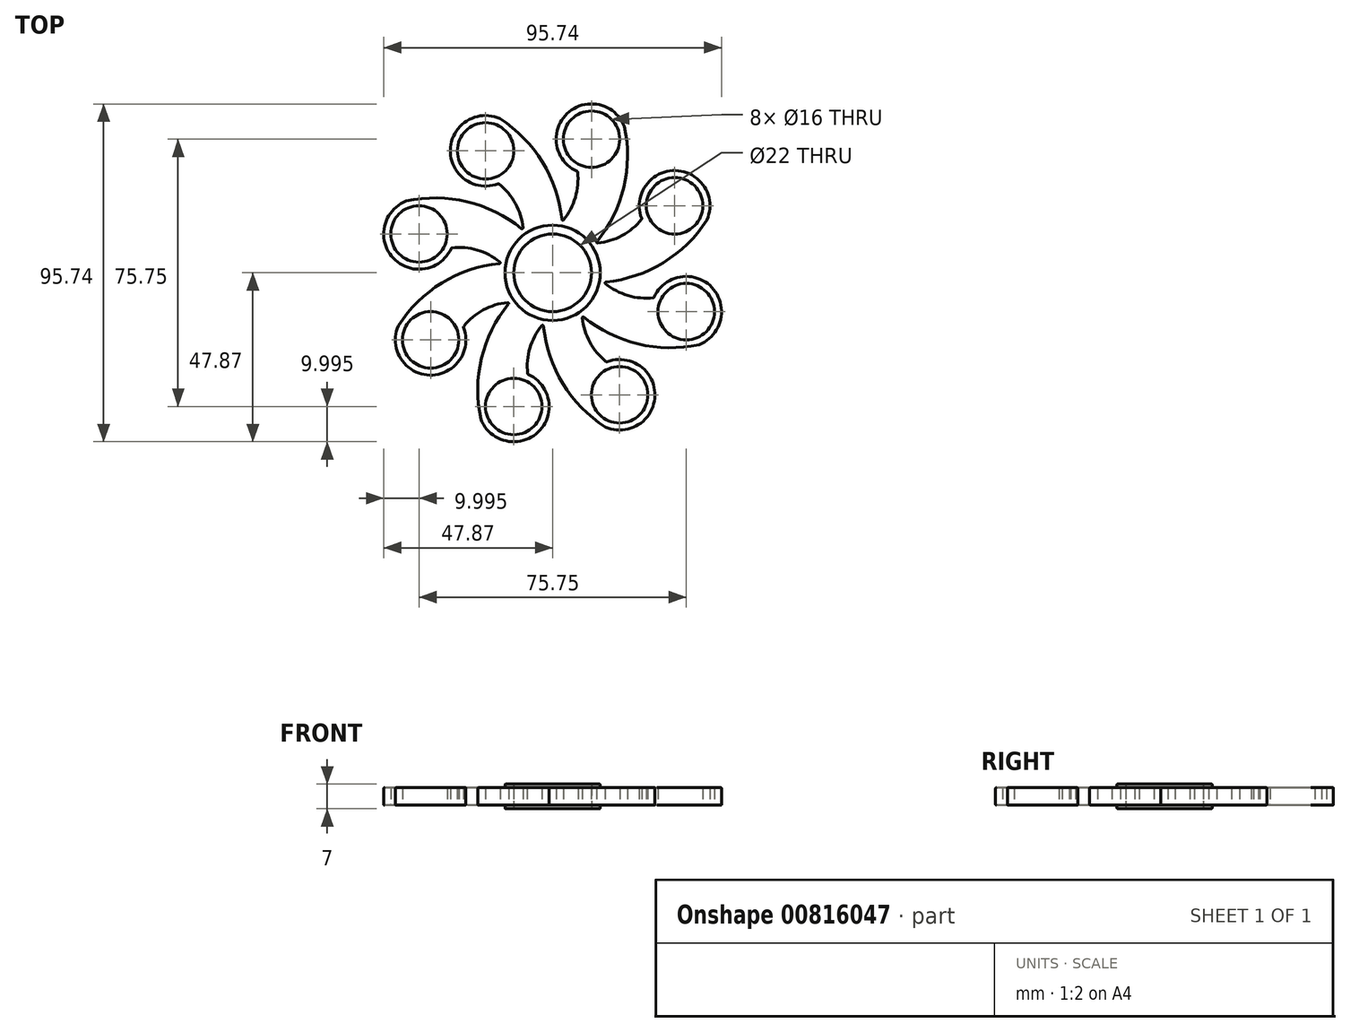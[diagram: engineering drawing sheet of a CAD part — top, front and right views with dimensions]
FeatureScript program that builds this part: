
annotation { "Feature Type Name" : "Feature", "Feature Type Description" : "" }
export const myFeature = defineFeature(function(context is Context, id is Id, definition is map)
    precondition{}
    {
        {
            var Q0;
            Q0=qCreatedBy(makeId("Top.planeOp"),FACE);
            var sketch = newSketch(context, id + "F0", { "sketchPlane" : qUnion([Q0])});
            skArc(sketch, "E0", {"start": v(-1.64, 10.88) * mm, "mid": v(-7.34, 8.2) * mm, "end": v(-10.63, 2.82) * mm});
            skCircle(sketch, "E1", {"center": v(0, 0) * mm, "radius": 11 * mm});
            skCircle(sketch, "E2", {"center": v(11.02, 37.87) * mm, "radius": 8 * mm});
            skPoint(sketch, "E3.start.orphan", {"position": v(0, 46.5) * mm});
            skArc(sketch, "E4", {"start": v(20.34, 41.5) * mm, "mid": v(4.08, 45.07) * mm, "end": v(7.06, 28.7) * mm});
            skArc(sketch, "E5", {"start": v(12.14, 8.36) * mm, "mid": v(20.1, 23.97) * mm, "end": v(20.34, 41.5) * mm});
            skArc(sketch, "E6", {"start": v(2.68, 14.5) * mm, "mid": v(6.38, 21.13) * mm, "end": v(7.06, 28.7) * mm});
            skArc(sketch, "E7.1.0", {"start": v(-14.96, 43.72) * mm, "mid": v(-29, 34.75) * mm, "end": v(-15.3, 25.28) * mm});
            skArc(sketch, "E7.1.1", {"start": v(2.68, 14.5) * mm, "mid": v(-2.74, 31.16) * mm, "end": v(-14.96, 43.72) * mm});
            skArc(sketch, "E7.1.2", {"start": v(-8.36, 12.14) * mm, "mid": v(-10.43, 19.45) * mm, "end": v(-15.3, 25.28) * mm});
            skCircle(sketch, "E7.1.3", {"center": v(-19, 34.57) * mm, "radius": 8 * mm});
            skArc(sketch, "E7.2.0", {"start": v(-41.5, 20.34) * mm, "mid": v(-45.07, 4.08) * mm, "end": v(-28.7, 7.06) * mm});
            skArc(sketch, "E7.2.1", {"start": v(-8.36, 12.14) * mm, "mid": v(-23.97, 20.1) * mm, "end": v(-41.5, 20.34) * mm});
            skArc(sketch, "E7.2.2", {"start": v(-14.5, 2.68) * mm, "mid": v(-21.13, 6.38) * mm, "end": v(-28.7, 7.06) * mm});
            skCircle(sketch, "E7.2.3", {"center": v(-37.87, 11.02) * mm, "radius": 8 * mm});
            skArc(sketch, "E7.3.0", {"start": v(-43.72, -14.96) * mm, "mid": v(-34.75, -29) * mm, "end": v(-25.28, -15.3) * mm});
            skArc(sketch, "E7.3.1", {"start": v(-14.5, 2.68) * mm, "mid": v(-31.16, -2.74) * mm, "end": v(-43.72, -14.96) * mm});
            skArc(sketch, "E7.3.2", {"start": v(-12.14, -8.36) * mm, "mid": v(-19.45, -10.43) * mm, "end": v(-25.28, -15.3) * mm});
            skCircle(sketch, "E7.3.3", {"center": v(-34.57, -19) * mm, "radius": 8 * mm});
            skArc(sketch, "E7.4.0", {"start": v(-20.34, -41.5) * mm, "mid": v(-4.08, -45.07) * mm, "end": v(-7.06, -28.7) * mm});
            skArc(sketch, "E7.4.1", {"start": v(-12.14, -8.36) * mm, "mid": v(-20.1, -23.97) * mm, "end": v(-20.34, -41.5) * mm});
            skArc(sketch, "E7.4.2", {"start": v(-2.68, -14.5) * mm, "mid": v(-6.38, -21.13) * mm, "end": v(-7.06, -28.7) * mm});
            skCircle(sketch, "E7.4.3", {"center": v(-11.02, -37.87) * mm, "radius": 8 * mm});
            skArc(sketch, "E7.5.0", {"start": v(14.96, -43.72) * mm, "mid": v(29, -34.75) * mm, "end": v(15.3, -25.28) * mm});
            skArc(sketch, "E7.5.1", {"start": v(-2.68, -14.5) * mm, "mid": v(2.74, -31.16) * mm, "end": v(14.96, -43.72) * mm});
            skArc(sketch, "E7.5.2", {"start": v(8.36, -12.14) * mm, "mid": v(10.43, -19.45) * mm, "end": v(15.3, -25.28) * mm});
            skCircle(sketch, "E7.5.3", {"center": v(19, -34.57) * mm, "radius": 8 * mm});
            skArc(sketch, "E7.6.0", {"start": v(41.5, -20.34) * mm, "mid": v(45.07, -4.08) * mm, "end": v(28.7, -7.06) * mm});
            skArc(sketch, "E7.6.1", {"start": v(8.36, -12.14) * mm, "mid": v(23.97, -20.1) * mm, "end": v(41.5, -20.34) * mm});
            skArc(sketch, "E7.6.2", {"start": v(14.5, -2.68) * mm, "mid": v(21.13, -6.38) * mm, "end": v(28.7, -7.06) * mm});
            skCircle(sketch, "E7.6.3", {"center": v(37.87, -11.02) * mm, "radius": 8 * mm});
            skArc(sketch, "E7.7.0", {"start": v(43.72, 14.96) * mm, "mid": v(34.75, 29) * mm, "end": v(25.28, 15.3) * mm});
            skArc(sketch, "E7.7.1", {"start": v(14.5, -2.68) * mm, "mid": v(31.16, 2.74) * mm, "end": v(43.72, 14.96) * mm});
            skArc(sketch, "E7.7.2", {"start": v(12.14, 8.36) * mm, "mid": v(19.45, 10.43) * mm, "end": v(25.28, 15.3) * mm});
            skCircle(sketch, "E7.7.3", {"center": v(34.57, 19) * mm, "radius": 8 * mm});
            skArc(sketch, "E8.trimOffspring", {"start": v(-8.85, 6.53) * mm, "mid": v(-9.92, 4.76) * mm, "end": v(-10.63, 2.82) * mm});
            skArc(sketch, "E9.trimOffspring", {"start": v(-10.88, -1.64) * mm, "mid": v(10.98, -0.6) * mm, "end": v(-10.63, 2.82) * mm});
            skArc(sketch, "E10.trimOffspring", {"start": v(-6.53, -8.85) * mm, "mid": v(8.2, 7.34) * mm, "end": v(-9.51, -5.53) * mm});
            skArc(sketch, "E11.trimOffspring", {"start": v(1.64, -10.88) * mm, "mid": v(0.6, 10.98) * mm, "end": v(-2.82, -10.63) * mm});
            skArc(sketch, "E12.trimOffspring", {"start": v(8.85, -6.53) * mm, "mid": v(4.76, 9.92) * mm, "end": v(-10.63, 2.82) * mm});
            skArc(sketch, "E13.trimOffspring", {"start": v(10.88, 1.64) * mm, "mid": v(0.6, 10.98) * mm, "end": v(-10.63, 2.82) * mm});
            skArc(sketch, "E14.trimOffspring", {"start": v(2.82, 10.63) * mm, "mid": v(-1.47, 10.9) * mm, "end": v(-5.53, 9.51) * mm});
            skArc(sketch, "E15.trimOffspring", {"start": v(-10.88, -1.64) * mm, "mid": v(-4.76, -9.92) * mm, "end": v(5.53, -9.51) * mm});
            skArc(sketch, "E16.trimOffspring", {"start": v(-10.88, -1.64) * mm, "mid": v(-0.6, -10.98) * mm, "end": v(10.63, -2.82) * mm});
            skSolve(sketch);
        }
        {
            var Q0;
            Q0 = qSketchRegion(id + "F0", true);
            extrude(context, id + "F1", {"entities" : qUnion([Q0]), "depth" : 5 * mm, "offsetDistance" : 25 * mm});
        }
        {
            var Q0;
            Q0=makeQuery(id+"F1.opExtrude","CAP_FACE",FACE,{"disambiguationData":[OSD([sQuery(id+"F0.wireOp",EDGE,"E1"),sQuery(id+"F0.wireOp",EDGE,"E2"),sQuery(id+"F0.wireOp",EDGE,"E4"),sQuery(id+"F0.wireOp",EDGE,"E5"),sQuery(id+"F0.wireOp",EDGE,"E6"),sQuery(id+"F0.wireOp",EDGE,"E7.1.0"),sQuery(id+"F0.wireOp",EDGE,"E7.1.1"),sQuery(id+"F0.wireOp",EDGE,"E7.1.2"),sQuery(id+"F0.wireOp",EDGE,"E7.1.3"),sQuery(id+"F0.wireOp",EDGE,"E7.2.0"),sQuery(id+"F0.wireOp",EDGE,"E7.2.1"),sQuery(id+"F0.wireOp",EDGE,"E7.2.2"),sQuery(id+"F0.wireOp",EDGE,"E7.2.3"),sQuery(id+"F0.wireOp",EDGE,"E7.3.0"),sQuery(id+"F0.wireOp",EDGE,"E7.3.1"),sQuery(id+"F0.wireOp",EDGE,"E7.3.2"),sQuery(id+"F0.wireOp",EDGE,"E7.3.3"),sQuery(id+"F0.wireOp",EDGE,"E7.4.0"),sQuery(id+"F0.wireOp",EDGE,"E7.4.1"),sQuery(id+"F0.wireOp",EDGE,"E7.4.2"),sQuery(id+"F0.wireOp",EDGE,"E7.4.3"),sQuery(id+"F0.wireOp",EDGE,"E7.5.0"),sQuery(id+"F0.wireOp",EDGE,"E7.5.1"),sQuery(id+"F0.wireOp",EDGE,"E7.5.2"),sQuery(id+"F0.wireOp",EDGE,"E7.5.3"),sQuery(id+"F0.wireOp",EDGE,"E7.6.0"),sQuery(id+"F0.wireOp",EDGE,"E7.6.1"),sQuery(id+"F0.wireOp",EDGE,"E7.6.2"),sQuery(id+"F0.wireOp",EDGE,"E7.6.3"),sQuery(id+"F0.wireOp",EDGE,"E7.7.0"),sQuery(id+"F0.wireOp",EDGE,"E7.7.1"),sQuery(id+"F0.wireOp",EDGE,"E7.7.2"),sQuery(id+"F0.wireOp",EDGE,"E7.7.3")])],"isStart":false});
            var sketch = newSketch(context, id + "F2", { "sketchPlane" : qUnion([Q0])});
            skCircle(sketch, "E17", {"center": v(0, 0) * mm, "radius": 11 * mm});
            skCircle(sketch, "E18", {"center": v(0, 0) * mm, "radius": 13.5 * mm});
            skSolve(sketch);
        }
        {
            var Q0;
            Q0 = qSketchRegion(id + "F2", true);
            extrude(context, id + "F3", {"entities" : qUnion([Q0]), "operationType" : NewBodyOperationType.ADD, "depth" : 1 * mm, "offsetDistance" : 25 * mm});
        }
        {
            var Q0;
            Q0=makeQuery(id+"F1.opExtrude","CAP_FACE",FACE,{"disambiguationData":[OSD([sQuery(id+"F0.wireOp",EDGE,"E1"),sQuery(id+"F0.wireOp",EDGE,"E2"),sQuery(id+"F0.wireOp",EDGE,"E4"),sQuery(id+"F0.wireOp",EDGE,"E5"),sQuery(id+"F0.wireOp",EDGE,"E6"),sQuery(id+"F0.wireOp",EDGE,"E7.1.0"),sQuery(id+"F0.wireOp",EDGE,"E7.1.1"),sQuery(id+"F0.wireOp",EDGE,"E7.1.2"),sQuery(id+"F0.wireOp",EDGE,"E7.1.3"),sQuery(id+"F0.wireOp",EDGE,"E7.2.0"),sQuery(id+"F0.wireOp",EDGE,"E7.2.1"),sQuery(id+"F0.wireOp",EDGE,"E7.2.2"),sQuery(id+"F0.wireOp",EDGE,"E7.2.3"),sQuery(id+"F0.wireOp",EDGE,"E7.3.0"),sQuery(id+"F0.wireOp",EDGE,"E7.3.1"),sQuery(id+"F0.wireOp",EDGE,"E7.3.2"),sQuery(id+"F0.wireOp",EDGE,"E7.3.3"),sQuery(id+"F0.wireOp",EDGE,"E7.4.0"),sQuery(id+"F0.wireOp",EDGE,"E7.4.1"),sQuery(id+"F0.wireOp",EDGE,"E7.4.2"),sQuery(id+"F0.wireOp",EDGE,"E7.4.3"),sQuery(id+"F0.wireOp",EDGE,"E7.5.0"),sQuery(id+"F0.wireOp",EDGE,"E7.5.1"),sQuery(id+"F0.wireOp",EDGE,"E7.5.2"),sQuery(id+"F0.wireOp",EDGE,"E7.5.3"),sQuery(id+"F0.wireOp",EDGE,"E7.6.0"),sQuery(id+"F0.wireOp",EDGE,"E7.6.1"),sQuery(id+"F0.wireOp",EDGE,"E7.6.2"),sQuery(id+"F0.wireOp",EDGE,"E7.6.3"),sQuery(id+"F0.wireOp",EDGE,"E7.7.0"),sQuery(id+"F0.wireOp",EDGE,"E7.7.1"),sQuery(id+"F0.wireOp",EDGE,"E7.7.2"),sQuery(id+"F0.wireOp",EDGE,"E7.7.3")])],"isStart":true});
            var sketch = newSketch(context, id + "F4", { "sketchPlane" : qUnion([Q0])});
            skCircle(sketch, "E19", {"center": v(0, 0) * mm, "radius": 11 * mm});
            skCircle(sketch, "E20", {"center": v(0, 0) * mm, "radius": 13.5 * mm});
            skSolve(sketch);
        }
        {
            var Q0;
            Q0 = qSketchRegion(id + "F4", true);
            extrude(context, id + "F5", {"entities" : qUnion([Q0]), "operationType" : NewBodyOperationType.ADD, "depth" : 1 * mm, "offsetDistance" : 25 * mm});
        }
        {
            var Q0;
            Q0=makeQuery(id+"F1.opExtrude","SWEPT_FACE",FACE,{"disambiguationData":[OSD([sQuery(id+"F0.wireOp",EDGE,"E7.7.0")])]});
            var Q1;
            Q1=makeQuery(id+"F1.opExtrude","CAP_EDGE",EDGE,{"disambiguationData":[OSD([sQuery(id+"F0.wireOp",EDGE,"E7.3.3")])],"isStart":false});
            var Q2;
            Q2=makeQuery(id+"F1.opExtrude","CAP_EDGE",EDGE,{"disambiguationData":[OSD([sQuery(id+"F0.wireOp",EDGE,"E7.6.0")])],"isStart":false});
            var Q3;
            Q3=makeQuery(id+"F1.opExtrude","CAP_EDGE",EDGE,{"disambiguationData":[OSD([sQuery(id+"F0.wireOp",EDGE,"E7.3.0")])],"isStart":false});
            var Q4;
            Q4=makeQuery(id+"F1.opExtrude","CAP_EDGE",EDGE,{"disambiguationData":[OSD([sQuery(id+"F0.wireOp",EDGE,"E7.4.2")])],"isStart":false});
            var Q5;
            Q5=makeQuery(id+"F1.opExtrude","CAP_EDGE",EDGE,{"disambiguationData":[OSD([sQuery(id+"F0.wireOp",EDGE,"E7.3.2")])],"isStart":false});
            var Q6;
            Q6=makeQuery(id+"F1.opExtrude","CAP_EDGE",EDGE,{"disambiguationData":[OSD([sQuery(id+"F0.wireOp",EDGE,"E7.1.0")])],"isStart":false});
            var Q7;
            Q7=makeQuery(id+"F1.opExtrude","CAP_EDGE",EDGE,{"disambiguationData":[OSD([sQuery(id+"F0.wireOp",EDGE,"E7.3.1")])],"isStart":false});
            var Q8;
            Q8=makeQuery(id+"F1.opExtrude","SWEPT_FACE",FACE,{"disambiguationData":[OSD([sQuery(id+"F0.wireOp",EDGE,"E7.3.0")])]});
            var Q9;
            Q9=makeQuery(id+"F1.opExtrude","CAP_EDGE",EDGE,{"disambiguationData":[OSD([sQuery(id+"F0.wireOp",EDGE,"E7.5.2")])],"isStart":false});
            var Q10;
            Q10=makeQuery(id+"F1.opExtrude","SWEPT_FACE",FACE,{"disambiguationData":[OSD([sQuery(id+"F0.wireOp",EDGE,"E5")])]});
            var Q11;
            Q11=makeQuery(id+"F1.opExtrude","SWEPT_FACE",FACE,{"disambiguationData":[OSD([sQuery(id+"F0.wireOp",EDGE,"E7.4.3")])]});
            var Q12;
            Q12=makeQuery(id+"F3.opExtrude","CAP_EDGE",EDGE,{"disambiguationData":[OSD([sQuery(id+"F2.wireOp",EDGE,"E18")])],"isStart":false});
            var Q13;
            Q13=makeQuery(id+"F1.opExtrude","SWEPT_FACE",FACE,{"disambiguationData":[OSD([sQuery(id+"F0.wireOp",EDGE,"E7.6.1")])]});
            var Q14;
            Q14=makeQuery(id+"F1.opExtrude","SWEPT_FACE",FACE,{"disambiguationData":[OSD([sQuery(id+"F0.wireOp",EDGE,"E7.5.0")])]});
            var Q15;
            Q15=makeQuery(id+"F3.opExtrude","SWEPT_FACE",FACE,{"disambiguationData":[OSD([sQuery(id+"F2.wireOp",EDGE,"E18")])]});
            var Q16;
            Q16=makeQuery(id+"F1.opExtrude","SWEPT_FACE",FACE,{"disambiguationData":[OSD([sQuery(id+"F0.wireOp",EDGE,"E7.3.3")])]});
            var Q17;
            Q17=makeQuery(id+"F1.opExtrude","SWEPT_FACE",FACE,{"disambiguationData":[OSD([sQuery(id+"F0.wireOp",EDGE,"E7.7.1")])]});
            var Q18;
            Q18=makeQuery(id+"F1.opExtrude","CAP_FACE",FACE,{"disambiguationData":[OSD([sQuery(id+"F0.wireOp",EDGE,"E1"),sQuery(id+"F0.wireOp",EDGE,"E2"),sQuery(id+"F0.wireOp",EDGE,"E4"),sQuery(id+"F0.wireOp",EDGE,"E5"),sQuery(id+"F0.wireOp",EDGE,"E6"),sQuery(id+"F0.wireOp",EDGE,"E7.1.0"),sQuery(id+"F0.wireOp",EDGE,"E7.1.1"),sQuery(id+"F0.wireOp",EDGE,"E7.1.2"),sQuery(id+"F0.wireOp",EDGE,"E7.1.3"),sQuery(id+"F0.wireOp",EDGE,"E7.2.0"),sQuery(id+"F0.wireOp",EDGE,"E7.2.1"),sQuery(id+"F0.wireOp",EDGE,"E7.2.2"),sQuery(id+"F0.wireOp",EDGE,"E7.2.3"),sQuery(id+"F0.wireOp",EDGE,"E7.3.0"),sQuery(id+"F0.wireOp",EDGE,"E7.3.1"),sQuery(id+"F0.wireOp",EDGE,"E7.3.2"),sQuery(id+"F0.wireOp",EDGE,"E7.3.3"),sQuery(id+"F0.wireOp",EDGE,"E7.4.0"),sQuery(id+"F0.wireOp",EDGE,"E7.4.1"),sQuery(id+"F0.wireOp",EDGE,"E7.4.2"),sQuery(id+"F0.wireOp",EDGE,"E7.4.3"),sQuery(id+"F0.wireOp",EDGE,"E7.5.0"),sQuery(id+"F0.wireOp",EDGE,"E7.5.1"),sQuery(id+"F0.wireOp",EDGE,"E7.5.2"),sQuery(id+"F0.wireOp",EDGE,"E7.5.3"),sQuery(id+"F0.wireOp",EDGE,"E7.6.0"),sQuery(id+"F0.wireOp",EDGE,"E7.6.1"),sQuery(id+"F0.wireOp",EDGE,"E7.6.2"),sQuery(id+"F0.wireOp",EDGE,"E7.6.3"),sQuery(id+"F0.wireOp",EDGE,"E7.7.0"),sQuery(id+"F0.wireOp",EDGE,"E7.7.1"),sQuery(id+"F0.wireOp",EDGE,"E7.7.2"),sQuery(id+"F0.wireOp",EDGE,"E7.7.3")])],"isStart":false});
            var Q19;
            Q19=makeQuery(id+"F1.opExtrude","SWEPT_FACE",FACE,{"disambiguationData":[OSD([sQuery(id+"F0.wireOp",EDGE,"E7.3.1")])]});
            var Q20;
            Q20=makeQuery(id+"F1.opExtrude","CAP_EDGE",EDGE,{"disambiguationData":[OSD([sQuery(id+"F0.wireOp",EDGE,"E7.7.2")])],"isStart":false});
            var Q21;
            Q21=makeQuery(id+"F1.opExtrude","CAP_EDGE",EDGE,{"disambiguationData":[OSD([sQuery(id+"F0.wireOp",EDGE,"E7.5.0")])],"isStart":false});
            var Q22;
            Q22=makeQuery(id+"F1.opExtrude","CAP_EDGE",EDGE,{"disambiguationData":[OSD([sQuery(id+"F0.wireOp",EDGE,"E7.1.1")])],"isStart":false});
            var Q23;
            Q23=makeQuery(id+"F1.opExtrude","CAP_EDGE",EDGE,{"disambiguationData":[OSD([sQuery(id+"F0.wireOp",EDGE,"E7.7.1")])],"isStart":false});
            var Q24;
            Q24=makeQuery(id+"F1.opExtrude","CAP_EDGE",EDGE,{"disambiguationData":[OSD([sQuery(id+"F0.wireOp",EDGE,"E7.6.1")])],"isStart":false});
            var Q25;
            Q25=makeQuery(id+"F1.opExtrude","CAP_EDGE",EDGE,{"disambiguationData":[OSD([sQuery(id+"F0.wireOp",EDGE,"E7.6.3")])],"isStart":false});
            var Q26;
            Q26=makeQuery(id+"F3.opExtrude","CAP_FACE",FACE,{"disambiguationData":[OSD([sQuery(id+"F2.wireOp",EDGE,"E17"),sQuery(id+"F2.wireOp",EDGE,"E18")])],"isStart":false});
            var Q27;
            Q27=makeQuery(id+"F1.opExtrude","SWEPT_FACE",FACE,{"disambiguationData":[OSD([sQuery(id+"F0.wireOp",EDGE,"E7.6.3")])]});
            var Q28;
            Q28=makeQuery(id+"F1.opExtrude","CAP_EDGE",EDGE,{"disambiguationData":[OSD([sQuery(id+"F0.wireOp",EDGE,"E7.4.1")])],"isStart":false});
            var Q29;
            Q29=makeQuery(id+"F1.opExtrude","SWEPT_FACE",FACE,{"disambiguationData":[OSD([sQuery(id+"F0.wireOp",EDGE,"E7.1.0")])]});
            var Q30;
            Q30=makeQuery(id+"F1.opExtrude","SWEPT_FACE",FACE,{"disambiguationData":[OSD([sQuery(id+"F0.wireOp",EDGE,"E7.6.0")])]});
            var Q31;
            Q31=makeQuery(id+"F1.opExtrude","SWEPT_FACE",FACE,{"disambiguationData":[OSD([sQuery(id+"F0.wireOp",EDGE,"E7.5.1")])]});
            var Q32;
            Q32=makeQuery(id+"F1.opExtrude","SWEPT_FACE",FACE,{"disambiguationData":[OSD([sQuery(id+"F0.wireOp",EDGE,"E7.4.0")])]});
            var Q33;
            Q33=makeQuery(id+"F1.opExtrude","SWEPT_FACE",FACE,{"disambiguationData":[OSD([sQuery(id+"F0.wireOp",EDGE,"E7.5.3")])]});
            var Q34;
            Q34=makeQuery(id+"F1.opExtrude","CAP_EDGE",EDGE,{"disambiguationData":[OSD([sQuery(id+"F0.wireOp",EDGE,"E7.2.1")])],"isStart":false});
            var Q35;
            Q35=makeQuery(id+"F1.opExtrude","SWEPT_FACE",FACE,{"disambiguationData":[OSD([sQuery(id+"F0.wireOp",EDGE,"E4")])]});
            var Q36;
            Q36=makeQuery(id+"F1.opExtrude","CAP_EDGE",EDGE,{"disambiguationData":[OSD([sQuery(id+"F0.wireOp",EDGE,"E4")])],"isStart":false});
            var Q37;
            Q37=makeQuery(id+"F1.opExtrude","SWEPT_FACE",FACE,{"disambiguationData":[OSD([sQuery(id+"F0.wireOp",EDGE,"E7.2.0")])]});
            var Q38;
            Q38=makeQuery(id+"F1.opExtrude","SWEPT_FACE",FACE,{"disambiguationData":[OSD([sQuery(id+"F0.wireOp",EDGE,"E7.2.3")])]});
            var Q39;
            Q39=makeQuery(id+"F1.opExtrude","SWEPT_FACE",FACE,{"disambiguationData":[OSD([sQuery(id+"F0.wireOp",EDGE,"E7.4.1")])]});
            var Q40;
            Q40=makeQuery(id+"F3.opExtrude","CAP_EDGE",EDGE,{"disambiguationData":[OSD([sQuery(id+"F2.wireOp",EDGE,"E17")])],"isStart":false});
            var Q41;
            Q41=makeQuery(id+"F1.opExtrude","CAP_EDGE",EDGE,{"disambiguationData":[OSD([sQuery(id+"F0.wireOp",EDGE,"E5")])],"isStart":false});
            var Q42;
            Q42=makeQuery(id+"F1.opExtrude","CAP_EDGE",EDGE,{"disambiguationData":[OSD([sQuery(id+"F0.wireOp",EDGE,"E7.6.2")])],"isStart":false});
            var Q43;
            Q43=makeQuery(id+"F1.opExtrude","CAP_EDGE",EDGE,{"disambiguationData":[OSD([sQuery(id+"F0.wireOp",EDGE,"E7.4.3")])],"isStart":false});
            var Q44;
            Q44=makeQuery(id+"F1.opExtrude","SWEPT_FACE",FACE,{"disambiguationData":[OSD([sQuery(id+"F0.wireOp",EDGE,"E7.1.1")])]});
            var Q45;
            Q45=makeQuery(id+"F1.opExtrude","CAP_EDGE",EDGE,{"disambiguationData":[OSD([sQuery(id+"F0.wireOp",EDGE,"E7.5.1")])],"isStart":false});
            var Q46;
            Q46=makeQuery(id+"F1.opExtrude","CAP_EDGE",EDGE,{"disambiguationData":[OSD([sQuery(id+"F0.wireOp",EDGE,"E6")])],"isStart":false});
            var Q47;
            Q47=makeQuery(id+"F1.opExtrude","SWEPT_FACE",FACE,{"disambiguationData":[OSD([sQuery(id+"F0.wireOp",EDGE,"E7.2.2")])]});
            var Q48;
            Q48=makeQuery(id+"F1.opExtrude","SWEPT_FACE",FACE,{"disambiguationData":[OSD([sQuery(id+"F0.wireOp",EDGE,"E6")])]});
            var Q49;
            Q49=makeQuery(id+"F1.opExtrude","CAP_EDGE",EDGE,{"disambiguationData":[OSD([sQuery(id+"F0.wireOp",EDGE,"E7.2.3")])],"isStart":false});
            var Q50;
            Q50=makeQuery(id+"F1.opExtrude","CAP_EDGE",EDGE,{"disambiguationData":[OSD([sQuery(id+"F0.wireOp",EDGE,"E7.6.0")])],"isStart":true});
            var Q51;
            Q51=makeQuery(id+"F1.opExtrude","CAP_EDGE",EDGE,{"disambiguationData":[OSD([sQuery(id+"F0.wireOp",EDGE,"E5")])],"isStart":true});
            var Q52;
            Q52=makeQuery(id+"F1.opExtrude","SWEPT_FACE",FACE,{"disambiguationData":[OSD([sQuery(id+"F0.wireOp",EDGE,"E7.7.3")])]});
            var Q53;
            Q53=makeQuery(id+"F1.opExtrude","CAP_EDGE",EDGE,{"disambiguationData":[OSD([sQuery(id+"F0.wireOp",EDGE,"E7.2.2")])],"isStart":false});
            var Q54;
            Q54=makeQuery(id+"F1.opExtrude","SWEPT_FACE",FACE,{"disambiguationData":[OSD([sQuery(id+"F0.wireOp",EDGE,"E7.7.2")])]});
            var Q55;
            Q55=makeQuery(id+"F1.opExtrude","SWEPT_EDGE",EDGE,{"disambiguationData":[OSD([sQuery(id+"F0.wireOp",EDGE,"E7.6.0"),sQuery(id+"F0.wireOp",EDGE,"E7.6.1")])]});
            var Q56;
            Q56=makeQuery(id+"F1.opExtrude","CAP_EDGE",EDGE,{"disambiguationData":[OSD([sQuery(id+"F0.wireOp",EDGE,"E7.3.3")])],"isStart":true});
            var Q57;
            Q57=makeQuery(id+"F1.opExtrude","SWEPT_EDGE",EDGE,{"disambiguationData":[OSD([sQuery(id+"F0.wireOp",EDGE,"E4"),sQuery(id+"F0.wireOp",EDGE,"E5")])]});
            var Q58;
            Q58=makeQuery(id+"F1.opExtrude","CAP_EDGE",EDGE,{"disambiguationData":[OSD([sQuery(id+"F0.wireOp",EDGE,"E7.6.3")])],"isStart":true});
            var Q59;
            Q59=makeQuery(id+"F1.opExtrude","CAP_FACE",FACE,{"disambiguationData":[OSD([sQuery(id+"F0.wireOp",EDGE,"E1"),sQuery(id+"F0.wireOp",EDGE,"E2"),sQuery(id+"F0.wireOp",EDGE,"E4"),sQuery(id+"F0.wireOp",EDGE,"E5"),sQuery(id+"F0.wireOp",EDGE,"E6"),sQuery(id+"F0.wireOp",EDGE,"E7.1.0"),sQuery(id+"F0.wireOp",EDGE,"E7.1.1"),sQuery(id+"F0.wireOp",EDGE,"E7.1.2"),sQuery(id+"F0.wireOp",EDGE,"E7.1.3"),sQuery(id+"F0.wireOp",EDGE,"E7.2.0"),sQuery(id+"F0.wireOp",EDGE,"E7.2.1"),sQuery(id+"F0.wireOp",EDGE,"E7.2.2"),sQuery(id+"F0.wireOp",EDGE,"E7.2.3"),sQuery(id+"F0.wireOp",EDGE,"E7.3.0"),sQuery(id+"F0.wireOp",EDGE,"E7.3.1"),sQuery(id+"F0.wireOp",EDGE,"E7.3.2"),sQuery(id+"F0.wireOp",EDGE,"E7.3.3"),sQuery(id+"F0.wireOp",EDGE,"E7.4.0"),sQuery(id+"F0.wireOp",EDGE,"E7.4.1"),sQuery(id+"F0.wireOp",EDGE,"E7.4.2"),sQuery(id+"F0.wireOp",EDGE,"E7.4.3"),sQuery(id+"F0.wireOp",EDGE,"E7.5.0"),sQuery(id+"F0.wireOp",EDGE,"E7.5.1"),sQuery(id+"F0.wireOp",EDGE,"E7.5.2"),sQuery(id+"F0.wireOp",EDGE,"E7.5.3"),sQuery(id+"F0.wireOp",EDGE,"E7.6.0"),sQuery(id+"F0.wireOp",EDGE,"E7.6.1"),sQuery(id+"F0.wireOp",EDGE,"E7.6.2"),sQuery(id+"F0.wireOp",EDGE,"E7.6.3"),sQuery(id+"F0.wireOp",EDGE,"E7.7.0"),sQuery(id+"F0.wireOp",EDGE,"E7.7.1"),sQuery(id+"F0.wireOp",EDGE,"E7.7.2"),sQuery(id+"F0.wireOp",EDGE,"E7.7.3")])],"isStart":true});
            var Q60;
            Q60=makeQuery(id+"F1.opExtrude","CAP_EDGE",EDGE,{"disambiguationData":[OSD([sQuery(id+"F0.wireOp",EDGE,"E7.5.0")])],"isStart":true});
            var Q61;
            Q61=makeQuery(id+"F1.opExtrude","SWEPT_FACE",FACE,{"disambiguationData":[OSD([sQuery(id+"F0.wireOp",EDGE,"E7.5.2")])]});
            var Q62;
            Q62=makeQuery(id+"F1.opExtrude","CAP_EDGE",EDGE,{"disambiguationData":[OSD([sQuery(id+"F0.wireOp",EDGE,"E7.1.1")])],"isStart":true});
            var Q63;
            Q63=makeQuery(id+"F1.opExtrude","SWEPT_FACE",FACE,{"disambiguationData":[OSD([sQuery(id+"F0.wireOp",EDGE,"E7.1.3")])]});
            var Q64;
            Q64=makeQuery(id+"F1.opExtrude","CAP_EDGE",EDGE,{"disambiguationData":[OSD([sQuery(id+"F0.wireOp",EDGE,"E7.4.3")])],"isStart":true});
            var Q65;
            Q65=makeQuery(id+"F5.boolean.opBoolean","MERGE",FACE,{"derivedFrom":[makeQuery(id+"F3.boolean.opBoolean","MERGE",FACE,{"derivedFrom":[makeQuery(id+"F1.opExtrude","SWEPT_FACE",FACE,{"disambiguationData":[OSD([sQuery(id+"F0.wireOp",EDGE,"E1")])]}),makeQuery(id+"F3.opExtrude","SWEPT_FACE",FACE,{"disambiguationData":[OSD([sQuery(id+"F2.wireOp",EDGE,"E17")])]})]}),makeQuery(id+"F5.opExtrude","SWEPT_FACE",FACE,{"disambiguationData":[OSD([sQuery(id+"F4.wireOp",EDGE,"E19")])]})]});
            var Q66;
            Q66=makeQuery(id+"F1.opExtrude","SWEPT_FACE",FACE,{"disambiguationData":[OSD([sQuery(id+"F0.wireOp",EDGE,"E2")])]});
            var Q67;
            Q67=makeQuery(id+"F1.opExtrude","CAP_EDGE",EDGE,{"disambiguationData":[OSD([sQuery(id+"F0.wireOp",EDGE,"E7.3.0")])],"isStart":true});
            var Q68;
            Q68=makeQuery(id+"F1.opExtrude","SWEPT_EDGE",EDGE,{"disambiguationData":[OSD([sQuery(id+"F0.wireOp",EDGE,"E7.3.0"),sQuery(id+"F0.wireOp",EDGE,"E7.3.1")])]});
            var Q69;
            Q69=makeQuery(id+"F1.opExtrude","CAP_EDGE",EDGE,{"disambiguationData":[OSD([sQuery(id+"F0.wireOp",EDGE,"E7.7.0")])],"isStart":false});
            var Q70;
            Q70=makeQuery(id+"F1.opExtrude","CAP_EDGE",EDGE,{"disambiguationData":[OSD([sQuery(id+"F0.wireOp",EDGE,"E7.2.1")])],"isStart":true});
            var Q71;
            Q71=makeQuery(id+"F1.opExtrude","CAP_EDGE",EDGE,{"disambiguationData":[OSD([sQuery(id+"F0.wireOp",EDGE,"E7.7.2")])],"isStart":true});
            var Q72;
            Q72=makeQuery(id+"F1.opExtrude","SWEPT_FACE",FACE,{"disambiguationData":[OSD([sQuery(id+"F0.wireOp",EDGE,"E7.3.2")])]});
            var Q73;
            Q73=makeQuery(id+"F1.opExtrude","SWEPT_EDGE",EDGE,{"disambiguationData":[OSD([sQuery(id+"F0.wireOp",EDGE,"E7.1.0"),sQuery(id+"F0.wireOp",EDGE,"E7.1.1")])]});
            var Q74;
            Q74=makeQuery(id+"F1.opExtrude","CAP_EDGE",EDGE,{"disambiguationData":[OSD([sQuery(id+"F0.wireOp",EDGE,"E7.5.1")])],"isStart":true});
            var Q75;
            Q75=makeQuery(id+"F1.opExtrude","CAP_EDGE",EDGE,{"disambiguationData":[OSD([sQuery(id+"F0.wireOp",EDGE,"E7.3.2")])],"isStart":true});
            var Q76;
            Q76=makeQuery(id+"F1.opExtrude","CAP_EDGE",EDGE,{"disambiguationData":[OSD([sQuery(id+"F0.wireOp",EDGE,"E7.4.1")])],"isStart":true});
            var Q77;
            Q77=makeQuery(id+"F1.opExtrude","CAP_EDGE",EDGE,{"disambiguationData":[OSD([sQuery(id+"F0.wireOp",EDGE,"E7.2.0")])],"isStart":false});
            var Q78;
            Q78=makeQuery(id+"F1.opExtrude","SWEPT_FACE",FACE,{"disambiguationData":[OSD([sQuery(id+"F0.wireOp",EDGE,"E7.1.2")])]});
            var Q79;
            Q79=makeQuery(id+"F1.opExtrude","CAP_EDGE",EDGE,{"disambiguationData":[OSD([sQuery(id+"F0.wireOp",EDGE,"E7.6.1")])],"isStart":true});
            var Q80;
            Q80=makeQuery(id+"F1.opExtrude","CAP_EDGE",EDGE,{"disambiguationData":[OSD([sQuery(id+"F0.wireOp",EDGE,"E7.3.1")])],"isStart":true});
            var Q81;
            Q81=makeQuery(id+"F1.opExtrude","CAP_EDGE",EDGE,{"disambiguationData":[OSD([sQuery(id+"F0.wireOp",EDGE,"E7.5.3")])],"isStart":false});
            var Q82;
            Q82=makeQuery(id+"F1.opExtrude","SWEPT_EDGE",EDGE,{"disambiguationData":[OSD([sQuery(id+"F0.wireOp",EDGE,"E7.4.0"),sQuery(id+"F0.wireOp",EDGE,"E7.4.1")])]});
            var Q83;
            Q83=makeQuery(id+"F1.opExtrude","SWEPT_FACE",FACE,{"disambiguationData":[OSD([sQuery(id+"F0.wireOp",EDGE,"E7.4.2")])]});
            var Q84;
            Q84=makeQuery(id+"F1.opExtrude","CAP_EDGE",EDGE,{"disambiguationData":[OSD([sQuery(id+"F0.wireOp",EDGE,"E7.1.0")])],"isStart":true});
            var Q85;
            Q85=makeQuery(id+"F5.opExtrude","CAP_EDGE",EDGE,{"disambiguationData":[OSD([sQuery(id+"F4.wireOp",EDGE,"E19")])],"isStart":false});
            var Q86;
            Q86=makeQuery(id+"F1.opExtrude","CAP_EDGE",EDGE,{"disambiguationData":[OSD([sQuery(id+"F0.wireOp",EDGE,"E7.1.3")])],"isStart":false});
            var Q87;
            Q87=makeQuery(id+"F1.opExtrude","CAP_EDGE",EDGE,{"disambiguationData":[OSD([sQuery(id+"F0.wireOp",EDGE,"E7.7.1")])],"isStart":true});
            var Q88;
            Q88=makeQuery(id+"F1.opExtrude","CAP_EDGE",EDGE,{"disambiguationData":[OSD([sQuery(id+"F0.wireOp",EDGE,"E7.4.0")])],"isStart":false});
            var Q89;
            Q89=makeQuery(id+"F1.opExtrude","SWEPT_FACE",FACE,{"disambiguationData":[OSD([sQuery(id+"F0.wireOp",EDGE,"E7.2.1")])]});
            var Q90;
            Q90=makeQuery(id+"F3.opExtrude","CAP_EDGE",EDGE,{"disambiguationData":[OSD([sQuery(id+"F2.wireOp",EDGE,"E18")])],"isStart":true});
            var Q91;
            Q91=makeQuery(id+"F1.opExtrude","CAP_EDGE",EDGE,{"disambiguationData":[OSD([sQuery(id+"F0.wireOp",EDGE,"E7.7.3")])],"isStart":false});
            var Q92;
            Q92=makeQuery(id+"F1.opExtrude","SWEPT_EDGE",EDGE,{"disambiguationData":[OSD([sQuery(id+"F0.wireOp",EDGE,"E7.5.0"),sQuery(id+"F0.wireOp",EDGE,"E7.5.1")])]});
            var Q93;
            Q93=makeQuery(id+"F1.opExtrude","CAP_EDGE",EDGE,{"disambiguationData":[OSD([sQuery(id+"F0.wireOp",EDGE,"E7.5.2")])],"isStart":true});
            var Q94;
            Q94=makeQuery(id+"F1.opExtrude","SWEPT_FACE",FACE,{"disambiguationData":[OSD([sQuery(id+"F0.wireOp",EDGE,"E7.6.2")])]});
            var Q95;
            Q95=makeQuery(id+"F1.opExtrude","CAP_EDGE",EDGE,{"disambiguationData":[OSD([sQuery(id+"F0.wireOp",EDGE,"E7.1.2")])],"isStart":false});
            var Q96;
            Q96=makeQuery(id+"F1.opExtrude","CAP_EDGE",EDGE,{"disambiguationData":[OSD([sQuery(id+"F0.wireOp",EDGE,"E4")])],"isStart":true});
            var Q97;
            Q97=makeQuery(id+"F1.opExtrude","SWEPT_EDGE",EDGE,{"disambiguationData":[OSD([sQuery(id+"F0.wireOp",EDGE,"E7.2.0"),sQuery(id+"F0.wireOp",EDGE,"E7.2.2")])]});
            var Q98;
            Q98=makeQuery(id+"F1.opExtrude","CAP_EDGE",EDGE,{"disambiguationData":[OSD([sQuery(id+"F0.wireOp",EDGE,"E7.1.3")])],"isStart":true});
            var Q99;
            Q99=makeQuery(id+"F1.opExtrude","SWEPT_EDGE",EDGE,{"disambiguationData":[OSD([sQuery(id+"F0.wireOp",EDGE,"E6"),sQuery(id+"F0.wireOp",EDGE,"E7.1.1")])]});
            var Q100;
            Q100=makeQuery(id+"F1.opExtrude","CAP_EDGE",EDGE,{"disambiguationData":[OSD([sQuery(id+"F0.wireOp",EDGE,"E7.2.2")])],"isStart":true});
            var Q101;
            Q101=makeQuery(id+"F1.opExtrude","SWEPT_EDGE",EDGE,{"disambiguationData":[OSD([sQuery(id+"F0.wireOp",EDGE,"E7.1.0"),sQuery(id+"F0.wireOp",EDGE,"E7.1.2")])]});
            var Q102;
            Q102=makeQuery(id+"F1.opExtrude","CAP_EDGE",EDGE,{"disambiguationData":[OSD([sQuery(id+"F0.wireOp",EDGE,"E7.7.0")])],"isStart":true});
            var Q103;
            Q103=makeQuery(id+"F5.opExtrude","CAP_FACE",FACE,{"disambiguationData":[OSD([sQuery(id+"F4.wireOp",EDGE,"E19"),sQuery(id+"F4.wireOp",EDGE,"E20")])],"isStart":false});
            var Q104;
            Q104=makeQuery(id+"F1.opExtrude","SWEPT_EDGE",EDGE,{"disambiguationData":[OSD([sQuery(id+"F0.wireOp",EDGE,"E7.7.0"),sQuery(id+"F0.wireOp",EDGE,"E7.7.1")])]});
            var Q105;
            Q105=makeQuery(id+"F1.opExtrude","SWEPT_EDGE",EDGE,{"disambiguationData":[OSD([sQuery(id+"F0.wireOp",EDGE,"E7.6.2"),sQuery(id+"F0.wireOp",EDGE,"E7.7.1")])]});
            var Q106;
            Q106=makeQuery(id+"F1.opExtrude","CAP_EDGE",EDGE,{"disambiguationData":[OSD([sQuery(id+"F0.wireOp",EDGE,"E7.6.2")])],"isStart":true});
            var Q107;
            Q107=makeQuery(id+"F1.opExtrude","SWEPT_EDGE",EDGE,{"disambiguationData":[OSD([sQuery(id+"F0.wireOp",EDGE,"E7.2.0"),sQuery(id+"F0.wireOp",EDGE,"E7.2.1")])]});
            var Q108;
            Q108=makeQuery(id+"F1.opExtrude","SWEPT_EDGE",EDGE,{"disambiguationData":[OSD([sQuery(id+"F0.wireOp",EDGE,"E7.6.0"),sQuery(id+"F0.wireOp",EDGE,"E7.6.2")])]});
            var Q109;
            Q109=makeQuery(id+"F1.opExtrude","SWEPT_EDGE",EDGE,{"disambiguationData":[OSD([sQuery(id+"F0.wireOp",EDGE,"E7.3.2"),sQuery(id+"F0.wireOp",EDGE,"E7.4.1")])]});
            var Q110;
            Q110=makeQuery(id+"F1.opExtrude","CAP_EDGE",EDGE,{"disambiguationData":[OSD([sQuery(id+"F0.wireOp",EDGE,"E7.4.2")])],"isStart":true});
            var Q111;
            Q111=makeQuery(id+"F1.opExtrude","SWEPT_EDGE",EDGE,{"disambiguationData":[OSD([sQuery(id+"F0.wireOp",EDGE,"E7.1.2"),sQuery(id+"F0.wireOp",EDGE,"E7.2.1")])]});
            var Q112;
            Q112=makeQuery(id+"F1.opExtrude","CAP_EDGE",EDGE,{"disambiguationData":[OSD([sQuery(id+"F0.wireOp",EDGE,"E6")])],"isStart":true});
            var Q113;
            Q113=makeQuery(id+"F1.opExtrude","CAP_EDGE",EDGE,{"disambiguationData":[OSD([sQuery(id+"F0.wireOp",EDGE,"E7.2.0")])],"isStart":true});
            var Q114;
            Q114=makeQuery(id+"F1.opExtrude","SWEPT_EDGE",EDGE,{"disambiguationData":[OSD([sQuery(id+"F0.wireOp",EDGE,"E7.7.0"),sQuery(id+"F0.wireOp",EDGE,"E7.7.2")])]});
            var Q115;
            Q115=makeQuery(id+"F1.opExtrude","SWEPT_EDGE",EDGE,{"disambiguationData":[OSD([sQuery(id+"F0.wireOp",EDGE,"E7.5.0"),sQuery(id+"F0.wireOp",EDGE,"E7.5.2")])]});
            var Q116;
            Q116=makeQuery(id+"F1.opExtrude","CAP_EDGE",EDGE,{"disambiguationData":[OSD([sQuery(id+"F0.wireOp",EDGE,"E2")])],"isStart":false});
            var Q117;
            Q117=makeQuery(id+"F1.opExtrude","CAP_EDGE",EDGE,{"disambiguationData":[OSD([sQuery(id+"F0.wireOp",EDGE,"E7.2.3")])],"isStart":true});
            var Q118;
            Q118=makeQuery(id+"F1.opExtrude","SWEPT_EDGE",EDGE,{"disambiguationData":[OSD([sQuery(id+"F0.wireOp",EDGE,"E7.4.2"),sQuery(id+"F0.wireOp",EDGE,"E7.5.1")])]});
            var Q119;
            Q119=makeQuery(id+"F1.opExtrude","SWEPT_EDGE",EDGE,{"disambiguationData":[OSD([sQuery(id+"F0.wireOp",EDGE,"E7.2.2"),sQuery(id+"F0.wireOp",EDGE,"E7.3.1")])]});
            var Q120;
            Q120=makeQuery(id+"F5.opExtrude","SWEPT_FACE",FACE,{"disambiguationData":[OSD([sQuery(id+"F4.wireOp",EDGE,"E20")])]});
            var Q121;
            Q121=makeQuery(id+"F1.opExtrude","CAP_EDGE",EDGE,{"disambiguationData":[OSD([sQuery(id+"F0.wireOp",EDGE,"E7.1.2")])],"isStart":true});
            var Q122;
            Q122=makeQuery(id+"F1.opExtrude","SWEPT_EDGE",EDGE,{"disambiguationData":[OSD([sQuery(id+"F0.wireOp",EDGE,"E5"),sQuery(id+"F0.wireOp",EDGE,"E7.7.2")])]});
            var Q123;
            Q123=makeQuery(id+"F1.opExtrude","SWEPT_EDGE",EDGE,{"disambiguationData":[OSD([sQuery(id+"F0.wireOp",EDGE,"E4"),sQuery(id+"F0.wireOp",EDGE,"E6")])]});
            var Q124;
            Q124=makeQuery(id+"F5.opExtrude","CAP_EDGE",EDGE,{"disambiguationData":[OSD([sQuery(id+"F4.wireOp",EDGE,"E20")])],"isStart":true});
            var Q125;
            Q125=makeQuery(id+"F1.opExtrude","SWEPT_EDGE",EDGE,{"disambiguationData":[OSD([sQuery(id+"F0.wireOp",EDGE,"E7.4.0"),sQuery(id+"F0.wireOp",EDGE,"E7.4.2")])]});
            var Q126;
            Q126=makeQuery(id+"F1.opExtrude","SWEPT_EDGE",EDGE,{"disambiguationData":[OSD([sQuery(id+"F0.wireOp",EDGE,"E7.3.0"),sQuery(id+"F0.wireOp",EDGE,"E7.3.2")])]});
            var Q127;
            Q127=makeQuery(id+"F1.opExtrude","CAP_EDGE",EDGE,{"disambiguationData":[OSD([sQuery(id+"F0.wireOp",EDGE,"E7.4.0")])],"isStart":true});
            var Q128;
            Q128=makeQuery(id+"F1.opExtrude","CAP_EDGE",EDGE,{"disambiguationData":[OSD([sQuery(id+"F0.wireOp",EDGE,"E7.7.3")])],"isStart":true});
            var Q129;
            Q129=makeQuery(id+"F1.opExtrude","CAP_EDGE",EDGE,{"disambiguationData":[OSD([sQuery(id+"F0.wireOp",EDGE,"E7.5.3")])],"isStart":true});
            var Q130;
            Q130=makeQuery(id+"F1.opExtrude","SWEPT_EDGE",EDGE,{"disambiguationData":[OSD([sQuery(id+"F0.wireOp",EDGE,"E7.5.2"),sQuery(id+"F0.wireOp",EDGE,"E7.6.1")])]});
            var Q131;
            Q131=makeQuery(id+"F5.opExtrude","CAP_EDGE",EDGE,{"disambiguationData":[OSD([sQuery(id+"F4.wireOp",EDGE,"E20")])],"isStart":false});
            var Q132;
            Q132=makeQuery(id+"F1.opExtrude","CAP_EDGE",EDGE,{"disambiguationData":[OSD([sQuery(id+"F0.wireOp",EDGE,"E2")])],"isStart":true});
            fillet(context, id + "F6", {"entities" : qUnion([Q0, Q1, Q2, Q3, Q4, Q5, Q6, Q7, Q8, Q9, Q10, Q11, Q12, Q13, Q14, Q15, Q16, Q17, Q18, Q19, Q20, Q21, Q22, Q23, Q24, Q25, Q26, Q27, Q28, Q29, Q30, Q31, Q32, Q33, Q34, Q35, Q36, Q37, Q38, Q39, Q40, Q41, Q42, Q43, Q44, Q45, Q46, Q47, Q48, Q49, Q50, Q51, Q52, Q53, Q54, Q55, Q56, Q57, Q58, Q59, Q60, Q61, Q62, Q63, Q64, Q65, Q66, Q67, Q68, Q69, Q70, Q71, Q72, Q73, Q74, Q75, Q76, Q77, Q78, Q79, Q80, Q81, Q82, Q83, Q84, Q85, Q86, Q87, Q88, Q89, Q90, Q91, Q92, Q93, Q94, Q95, Q96, Q97, Q98, Q99, Q100, Q101, Q102, Q103, Q104, Q105, Q106, Q107, Q108, Q109, Q110, Q111, Q112, Q113, Q114, Q115, Q116, Q117, Q118, Q119, Q120, Q121, Q122, Q123, Q124, Q125, Q126, Q127, Q128, Q129, Q130, Q131, Q132]), "radius" : 0.25 * mm, "tangentPropagation" : true, "allowEdgeOverflow" : false});
        }
    });
